# Revit family: LAMP_PLAT G3
name_source: partatom
category: Luminarias
revit_build: Autodesk Revit 2015 (Build: 20140606_1530(x64)
units: mm (PartAtom-declared; Revit-internal decimal feet)

## types (10) — shared parameters
CRI = 80
Cambio de temperatura de color de luz atenuada = <Ninguno>
Fabricante = LAMP
Filtro de color = 16777215
Finish = Matte Traffic White
Gear = Electronic
Height = 14 mm  [stored 0.0459318 ft]
IEE = A+
Insulation class = II
LED Lifetime = 50.000 L80 B10
Last update = 21/06/2018
Luminaire type = Indoor - Recessed and suspended luminaire
Lámpara = MID-POWER LED
MacAdam = 3
Manufacturer URL = http://www.lamp.es
Manufacturer country = Spain
Manufacturer name = LAMP
Material marco PLAT = LAMP_Acero Plat BL
Material marco empotrar = LAMP_Aluminio Plat BL
Plum = 31 W
Power = 28 W
Power Supply = 220-240V 50-60Hz
Product URL = http://www.lamp.es
Product datasheet = http://www.lamp.es
Separación luz = 20 mm  [stored 0.0656168 ft]
Type = MID POWER SAMSUNG
Weight = 3.90 kg
Ángulo de inclinación = 90.00°

## per-type parameters (varying)
- 600x600 3000 IP40 OPAL: A=596 mm  [stored 1.95538 ft]; A_1=554 mm  [stored 1.81759 ft]; A_2=526 mm  [stored 1.72572 ft]; A_3=526 mm  [stored 1.72572 ft]; A_Marco_1=600 mm; A_Marco_2=598 mm  [stored 1.96194 ft]; A_Susp=496 mm  [stored 1.6273 ft]; Archivo de red fotométrica=PL306035OP4030NW.IES; Descripción=PLAT G3 600X600 3400 WW OPAL IP40 WH; Dimensions=596x596x14; Efficacy=110 lm/W; Installation instructions=http://www.lamp.es; L=596 mm  [stored 1.95538 ft]; L_1=554 mm  [stored 1.81759 ft]; L_2=526 mm  [stored 1.72572 ft]; L_3=526 mm  [stored 1.72572 ft]; L_Marco_1=598 mm  [stored 1.96194 ft]; L_Marco_2=600 mm; L_Susp=496 mm  [stored 1.6273 ft]; Material difusor=LAMP_PC Difusor Opal Plat; Modelo=PL306035OP4030NW; Product code=PL306035OP4030NW; Protection rating=IP40 / IK06; Recessed dimensions=617x617x14
- 600x600 4000 IP40 OPAL: A=596 mm  [stored 1.95538 ft]; A_1=554 mm  [stored 1.81759 ft]; A_2=526 mm  [stored 1.72572 ft]; A_3=526 mm  [stored 1.72572 ft]; A_Marco_1=600 mm; A_Marco_2=598 mm  [stored 1.96194 ft]; A_Susp=496 mm  [stored 1.6273 ft]; Archivo de red fotométrica=PL306035OP4040NW.IES; Descripción=PLAT G3 600X600 3600 NW OPAL IP40 WH; Dimensions=596x596x14; Efficacy=116 lm/W; L=596 mm  [stored 1.95538 ft]; L_1=554 mm  [stored 1.81759 ft]; L_2=526 mm  [stored 1.72572 ft]; L_3=526 mm  [stored 1.72572 ft]; L_Marco_1=598 mm  [stored 1.96194 ft]; L_Marco_2=600 mm; L_Susp=496 mm  [stored 1.6273 ft]; Material difusor=LAMP_PC Difusor Opal Plat; Modelo=PL306035OP4040NW; Product code=PL306035OP4040NW; Protection rating=IP40 / IK06; Recessed dimensions=617x617x14
- 600x600 3000 IP54 OPAL: A=596 mm  [stored 1.95538 ft]; A_1=554 mm  [stored 1.81759 ft]; A_2=526 mm  [stored 1.72572 ft]; A_3=526 mm  [stored 1.72572 ft]; A_Marco_1=600 mm; A_Marco_2=598 mm  [stored 1.96194 ft]; A_Susp=496 mm  [stored 1.6273 ft]; Archivo de red fotométrica=PL306035OP5430NW.IES; Descripción=PLAT G3 600X600 3400 WW OPAL IP54 WH; Dimensions=596x596x14; Efficacy=110 lm/W; L=596 mm  [stored 1.95538 ft]; L_1=554 mm  [stored 1.81759 ft]; L_2=526 mm  [stored 1.72572 ft]; L_3=526 mm  [stored 1.72572 ft]; L_Marco_1=598 mm  [stored 1.96194 ft]; L_Marco_2=600 mm; L_Susp=496 mm  [stored 1.6273 ft]; Material difusor=LAMP_PC Difusor Opal Plat; Modelo=PL306035OP5430NW; Product code=PL306035OP5430NW; Protection rating=IP54 / IK06; Recessed dimensions=617x617x14
- 600x600 4000 IP54 OPAL: A=596 mm  [stored 1.95538 ft]; A_1=554 mm  [stored 1.81759 ft]; A_2=526 mm  [stored 1.72572 ft]; A_3=526 mm  [stored 1.72572 ft]; A_Marco_1=600 mm; A_Marco_2=598 mm  [stored 1.96194 ft]; A_Susp=496 mm  [stored 1.6273 ft]; Archivo de red fotométrica=PL306035OP5440NW.IES; Descripción=PLAT G3 600X600 3600 NW OPAL IP54 WH; Dimensions=596x596x14; Efficacy=116 lm/W; L=596 mm  [stored 1.95538 ft]; L_1=554 mm  [stored 1.81759 ft]; L_2=526 mm  [stored 1.72572 ft]; L_3=526 mm  [stored 1.72572 ft]; L_Marco_1=598 mm  [stored 1.96194 ft]; L_Marco_2=600 mm; L_Susp=496 mm  [stored 1.6273 ft]; Material difusor=LAMP_PC Difusor Opal Plat; Modelo=PL306035OP5440NW; Product code=PL306035OP5440NW; Protection rating=IP54 / IK06; Recessed dimensions=617x617x14
- 600x600 3000 IP40 PRIS: A=596 mm  [stored 1.95538 ft]; A_1=554 mm  [stored 1.81759 ft]; A_2=526 mm  [stored 1.72572 ft]; A_3=526 mm  [stored 1.72572 ft]; A_Marco_1=600 mm; A_Marco_2=598 mm  [stored 1.96194 ft]; A_Susp=496 mm  [stored 1.6273 ft]; Archivo de red fotométrica=PL306035PR4030NW.IES; Descripción=PLAT G3 600X600 3200 WW PRIS IP40 WH; Dimensions=596x596x14; Efficacy=103 lm/W; L=596 mm  [stored 1.95538 ft]; L_1=554 mm  [stored 1.81759 ft]; L_2=526 mm  [stored 1.72572 ft]; L_3=526 mm  [stored 1.72572 ft]; L_Marco_1=598 mm  [stored 1.96194 ft]; L_Marco_2=600 mm; L_Susp=496 mm  [stored 1.6273 ft]; Material difusor=LAMP_PC Difusor Prismático Plat; Modelo=PL306035PR4030NW; Product code=PL306035PR4030NW; Protection rating=IP40 / IK06; Recessed dimensions=617x617x14; UGR=19
- 600x600 4000 IP40 PRIS: A=596 mm  [stored 1.95538 ft]; A_1=554 mm  [stored 1.81759 ft]; A_2=526 mm  [stored 1.72572 ft]; A_3=526 mm  [stored 1.72572 ft]; A_Marco_1=600 mm; A_Marco_2=598 mm  [stored 1.96194 ft]; A_Susp=496 mm  [stored 1.6273 ft]; Archivo de red fotométrica=PL306035PR4040NW.IES; Descripción=PLAT G3 600X600 3400 NW PRIS IP40 WH; Dimensions=596x596x14; Efficacy=110 lm/W; L=596 mm  [stored 1.95538 ft]; L_1=554 mm  [stored 1.81759 ft]; L_2=526 mm  [stored 1.72572 ft]; L_3=526 mm  [stored 1.72572 ft]; L_Marco_1=598 mm  [stored 1.96194 ft]; L_Marco_2=600 mm; L_Susp=496 mm  [stored 1.6273 ft]; Material difusor=LAMP_PC Difusor Prismático Plat; Modelo=PL306035PR4040NW; Product code=PL306035PR4040NW; Protection rating=IP40 / IK06; Recessed dimensions=617x617x14; UGR=19
- 1200x300 3000 IP40 OPAL: A=296 mm  [stored 0.971129 ft]; A_1=254 mm; A_2=226 mm  [stored 0.74147 ft]; A_3=226 mm  [stored 0.74147 ft]; A_Marco_1=300 mm  [stored 0.984252 ft]; A_Marco_2=298 mm  [stored 0.97769 ft]; A_Susp=196 mm  [stored 0.643045 ft]; Archivo de red fotométrica=PL312035OP4030NW.IES; Descripción=PLAT G3 1200X300 3400 WW OPAL IP40 WH; Dimensions=1196x296x14; Efficacy=110 lm/W; L=1196 mm  [stored 3.92388 ft]; L_1=1154 mm  [stored 3.78609 ft]; L_2=1126 mm  [stored 3.69423 ft]; L_3=1126 mm  [stored 3.69423 ft]; L_Marco_1=1198 mm; L_Marco_2=1200 mm; L_Susp=1096 mm  [stored 3.5958 ft]; Material difusor=LAMP_PC Difusor Opal Plat; Modelo=PL312035OP4030NW; Product code=PL312035OP4030NW; Protection rating=IP40 / IK06; Recessed dimensions=1217x317x14
- 1200x300 4000 IP40 OPAL: A=296 mm  [stored 0.971129 ft]; A_1=254 mm; A_2=226 mm  [stored 0.74147 ft]; A_3=226 mm  [stored 0.74147 ft]; A_Marco_1=300 mm  [stored 0.984252 ft]; A_Marco_2=298 mm  [stored 0.97769 ft]; A_Susp=196 mm  [stored 0.643045 ft]; Archivo de red fotométrica=PL312035OP4040NW.IES; Descripción=PLAT G3 1200X300 3600 NW OPAL IP40 WH; Dimensions=1196x296x14; Efficacy=116 lm/W; L=1196 mm  [stored 3.92388 ft]; L_1=1154 mm  [stored 3.78609 ft]; L_2=1126 mm  [stored 3.69423 ft]; L_3=1126 mm  [stored 3.69423 ft]; L_Marco_1=1198 mm; L_Marco_2=1200 mm; L_Susp=1096 mm  [stored 3.5958 ft]; Material difusor=LAMP_PC Difusor Opal Plat; Modelo=PL312035OP4040NW; Product code=PL312035OP4040NW; Protection rating=IP40 / IK06; Recessed dimensions=1217x317x14
- 1200x300 3000 IP40 PRIS: A=296 mm  [stored 0.971129 ft]; A_1=254 mm; A_2=226 mm  [stored 0.74147 ft]; A_3=226 mm  [stored 0.74147 ft]; A_Marco_1=300 mm  [stored 0.984252 ft]; A_Marco_2=298 mm  [stored 0.97769 ft]; A_Susp=196 mm  [stored 0.643045 ft]; Archivo de red fotométrica=PL312035PR4030NW.IES; Descripción=PLAT G3 1200X300 3200 WW PRIS IP40 WH; Dimensions=1196x296x14; Efficacy=103 lm/W; L=1196 mm  [stored 3.92388 ft]; L_1=1154 mm  [stored 3.78609 ft]; L_2=1126 mm  [stored 3.69423 ft]; L_3=1126 mm  [stored 3.69423 ft]; L_Marco_1=1198 mm; L_Marco_2=1200 mm; L_Susp=1096 mm  [stored 3.5958 ft]; Material difusor=LAMP_PC Difusor Prismático Plat; Modelo=PL312035PR4030NW; Product code=PL312035PR4030NW; Protection rating=IP40 / IK06; Recessed dimensions=1217x317x14; UGR=19
- 1200x300 4000 IP40 PRIS: A=296 mm  [stored 0.971129 ft]; A_1=254 mm; A_2=226 mm  [stored 0.74147 ft]; A_3=226 mm  [stored 0.74147 ft]; A_Marco_1=300 mm  [stored 0.984252 ft]; A_Marco_2=298 mm  [stored 0.97769 ft]; A_Susp=196 mm  [stored 0.643045 ft]; Archivo de red fotométrica=PL312035PR4040NW.IES; Descripción=PLAT G3 1200X300 3200 WW PRIS IP40 WH; Dimensions=1196x296x14; Efficacy=103 lm/W; L=1196 mm  [stored 3.92388 ft]; L_1=1154 mm  [stored 3.78609 ft]; L_2=1126 mm  [stored 3.69423 ft]; L_3=1126 mm  [stored 3.69423 ft]; L_Marco_1=1198 mm; L_Marco_2=1200 mm; L_Susp=1096 mm  [stored 3.5958 ft]; Material difusor=LAMP_PC Difusor Prismático Plat; Modelo=PL312035PR4040NW; Product code=PL312035PR4040NW; Protection rating=IP40 / IK06; Recessed dimensions=1217x317x14; UGR=19

note: [stored X ft] marks values corroborated as IEEE doubles in the binary element streams (Revit-internal decimal feet)
